# Revit family: Опора фундаментная ФО-2
name_source: partatom
category: Обобщенные модели
units: mm (PartAtom-declared; Revit-internal decimal feet)

## family parameters
Всегда вертикально = Да
Может служить основой для арматурных стержней = Нет
На основе рабочей плоскости = Нет
Общий = Нет
При загрузке вырезать с полостями = Нет
Размер круглого соединителя = Использовать диаметр
Сохранять ориентацию аннотаций = Нет
Тип детали = Нормальный
Точка принадлежности помещению = Нет

## types (1)
- Опора фундаментная ФО-2
    ADSK_Размер_Высота = 550 мм
    ADSK_Размер_Длина = 750 мм
    ADSK_Размер_Ширина = 950 мм
    i боковушки по ширине = 0.273 :1
    Глубина выемки петли = 70 мм
    Глубина колодца = 450 мм
    Длина выемки петли = 160 мм
    Длина колодца по верху = 450 мм
    Длина колодца по низу = 360 мм
    Отметка по умолчанию = 0 мм
    Отступ петли = 110 мм
    Отступ подошвы выемки петли по ширине = 241 мм
    Размер_Длина по верху = 650 мм
    Размер_Ширина по верху = 650 мм
    Расстояние между петлями = 628 мм
    Скос выемки петли = 10 мм
    Фаска = 15 мм
    Ширина выемки петли = 110 мм
    Ширина колодца по верху = 350 мм
    Ширина колодца по низу = 260 мм
    высота_петли = 66 мм
    ширина_петли = 55 мм
